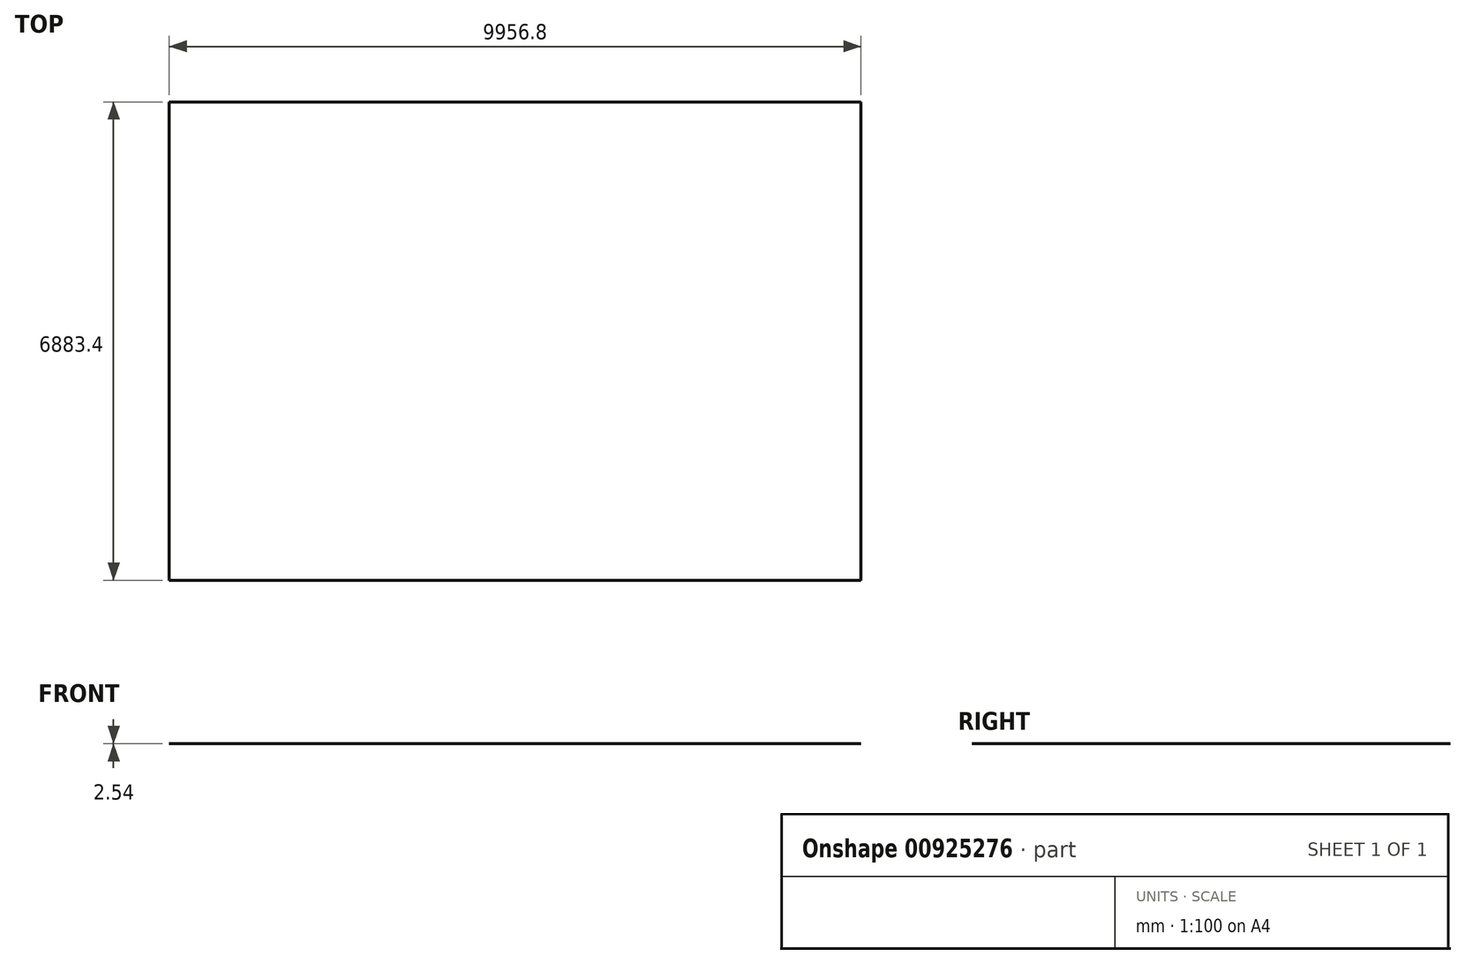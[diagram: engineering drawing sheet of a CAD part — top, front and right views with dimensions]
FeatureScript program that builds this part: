
annotation { "Feature Type Name" : "Feature", "Feature Type Description" : "" }
export const myFeature = defineFeature(function(context is Context, id is Id, definition is map)
    precondition{}
    {
        {
            var Q0;
            Q0=qCreatedBy(makeId("Top.planeOp"),FACE);
            var sketch = newSketch(context, id + "F0", { "sketchPlane" : qUnion([Q0])});
            skLineSegment(sketch, "E0.bottom", {"start": v(0, 0) * mm, "end": v(-9956.8, 0) * mm});
            skLineSegment(sketch, "E0.top", {"start": v(0, 6883.4) * mm, "end": v(-9956.8, 6883.4) * mm});
            skLineSegment(sketch, "E0.left", {"start": v(0, 0) * mm, "end": v(0, 6883.4) * mm});
            skLineSegment(sketch, "E0.right", {"start": v(-9956.8, 0) * mm, "end": v(-9956.8, 6883.4) * mm});
            skSolve(sketch);
        }
        {
            var Q0;
            Q0=makeQuery(id+"F0.imprint","IMPRINT",FACE,{"disambiguationData":[TD([[makeQuery(id+"F0.imprint","IMPRINT",EDGE,{"derivedFrom":sQuery(id+"F0.wireOp",EDGE,"E0.bottom")}),-1.0]])]});
            extrude(context, id + "F1", {"entities" : qUnion([Q0]), "depth" : 2.54 * mm, "offsetDistance" : 25.4 * mm});
        }
    });
